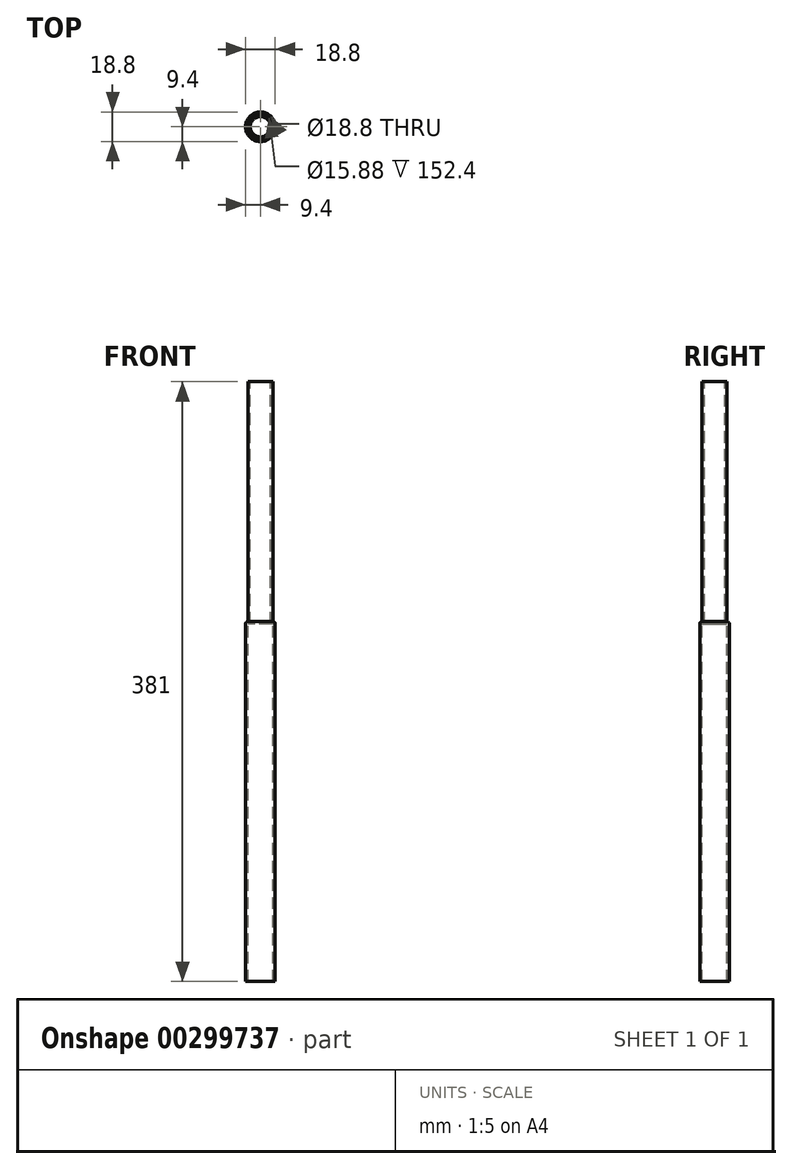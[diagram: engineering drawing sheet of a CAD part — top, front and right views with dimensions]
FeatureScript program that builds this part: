
annotation { "Feature Type Name" : "Feature", "Feature Type Description" : "" }
export const myFeature = defineFeature(function(context is Context, id is Id, definition is map)
    precondition{}
    {
        {
            var Q0;
            Q0=qCreatedBy(makeId("Front.planeOp"),FACE);
            var sketch = newSketch(context, id + "F0", { "sketchPlane" : qUnion([Q0])});
            skLineSegment(sketch, "E0", {"start": v(6.48, 381) * mm, "end": v(6.48, 227.14) * mm});
            skLineSegment(sketch, "E1", {"start": v(6.48, 227.14) * mm, "end": v(7.94, 227.14) * mm});
            skLineSegment(sketch, "E2", {"start": v(7.94, 227.14) * mm, "end": v(7.94, 0) * mm});
            skLineSegment(sketch, "E3", {"start": v(7.94, 0) * mm, "end": v(9.4, 0) * mm, "construction": true});
            skLineSegment(sketch, "E4", {"start": v(9.4, 0) * mm, "end": v(9.4, 228.6) * mm});
            skLineSegment(sketch, "E5", {"start": v(9.4, 228.6) * mm, "end": v(7.94, 228.6) * mm});
            skLineSegment(sketch, "E6", {"start": v(7.94, 228.6) * mm, "end": v(7.94, 381) * mm});
            skLineSegment(sketch, "E7", {"start": v(7.94, 381) * mm, "end": v(6.48, 381) * mm});
            skLineSegment(sketch, "E8", {"start": v(7.94, 228.6) * mm, "end": v(7.94, 227.14) * mm, "construction": true});
            skLineSegment(sketch, "E9", {"start": v(0, 0) * mm, "end": v(0, 76.21) * mm, "construction": true});
            skSolve(sketch);
        }
        {
            var Q0;
            Q0=sQuery(id+"F0.wireOp",EDGE,"E4");
            var Q1;
            Q1=sQuery(id+"F0.wireOp",EDGE,"E6");
            var Q2;
            Q2=sQuery(id+"F0.wireOp",EDGE,"E2");
            var Q3;
            Q3=sQuery(id+"F0.wireOp",EDGE,"E0");
            var Q4;
            Q4=sQuery(id+"F0.wireOp",EDGE,"E7");
            var Q5;
            Q5=sQuery(id+"F0.wireOp",EDGE,"E5");
            var Q6;
            Q6=sQuery(id+"F0.wireOp",EDGE,"E1");
            var Q7;
            Q7=sQuery(id+"F0.wireOp",EDGE,"E9");
            revolve(context, id + "F1", {"bodyType" : ToolBodyType.SURFACE, "surfaceEntities" : qUnion([Q0, Q1, Q2, Q3, Q4, Q5, Q6]), "axis" : qUnion([Q7]), "revolveType" : RevolveType.FULL});
        }
        {
            var Q0;
            Q0=makeQuery(id+"F1.opRevolve","SWEPT_EDGE",EDGE,{"disambiguationData":[OSD([sQuery(id+"F0.wireOp",VERTEX,"E5.start")])]});
            fillet(context, id + "F2", {"entities" : qUnion([Q0]), "radius" : 1.27 * mm, "tangentPropagation" : true, "allowEdgeOverflow" : false});
        }
    });
